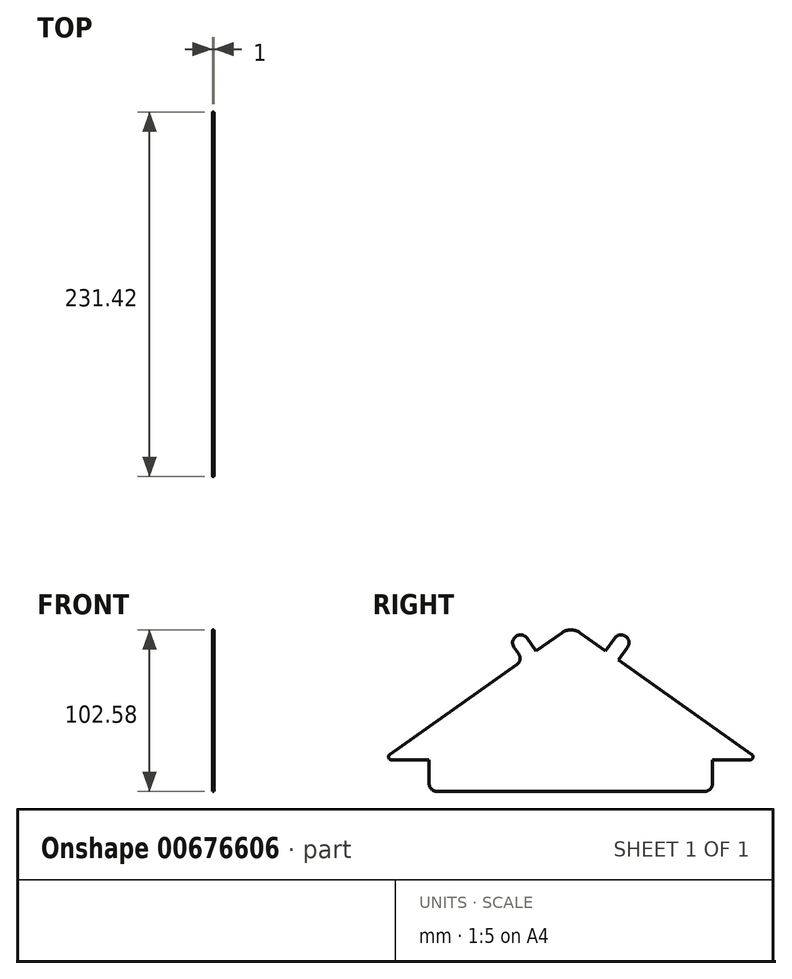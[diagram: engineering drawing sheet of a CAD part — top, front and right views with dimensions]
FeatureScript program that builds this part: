
annotation { "Feature Type Name" : "Feature", "Feature Type Description" : "" }
export const myFeature = defineFeature(function(context is Context, id is Id, definition is map)
    precondition{}
    {
        {
            var Q0;
            Q0=qCreatedBy(makeId("Right.planeOp"),FACE);
            var sketch = newSketch(context, id + "F0", { "sketchPlane" : qUnion([Q0])});
            skLineSegment(sketch, "E0", {"start": v(-120, 0) * mm, "end": v(120, 0) * mm, "construction": true});
            skLineSegment(sketch, "E1", {"start": v(120, 0) * mm, "end": v(0, 84.83) * mm});
            skLineSegment(sketch, "E2", {"start": v(0, 84.83) * mm, "end": v(-120, 0) * mm});
            skLineSegment(sketch, "E3", {"start": v(-120, 0) * mm, "end": v(-90, 0) * mm});
            skLineSegment(sketch, "E4", {"start": v(-90, 0) * mm, "end": v(-90, -20) * mm});
            skLineSegment(sketch, "E5", {"start": v(-90, -20) * mm, "end": v(90, -20) * mm});
            skLineSegment(sketch, "E6", {"start": v(90, -20) * mm, "end": v(90, 0) * mm});
            skLineSegment(sketch, "E7", {"start": v(90, 0) * mm, "end": v(120, 0) * mm});
            skSolve(sketch);
        }
        {
            var Q0;
            Q0 = qSketchRegion(id + "F0", true);
            extrude(context, id + "F1", {"entities" : qUnion([Q0]), "depth" : 1 * mm, "offsetDistance" : 25 * mm});
        }
        {
            var Q0;
            Q0=makeQuery(id+"F1.opExtrude","SWEPT_EDGE",EDGE,{"disambiguationData":[OSD([sQuery(id+"F0.wireOp",EDGE,"E4"),sQuery(id+"F0.wireOp",EDGE,"E5")])]});
            var Q1;
            Q1=makeQuery(id+"F1.opExtrude","SWEPT_EDGE",EDGE,{"disambiguationData":[OSD([sQuery(id+"F0.wireOp",EDGE,"E5"),sQuery(id+"F0.wireOp",EDGE,"E6")])]});
            fillet(context, id + "F2", {"entities" : qUnion([Q0, Q1]), "radius" : 5 * mm, "tangentPropagation" : true, "allowEdgeOverflow" : false});
        }
        {
            var Q0;
            Q0=makeQuery(id+"F1.opExtrude","SWEPT_EDGE",EDGE,{"disambiguationData":[OSD([sQuery(id+"F0.wireOp",EDGE,"E1"),sQuery(id+"F0.wireOp",EDGE,"E7")])]});
            var Q1;
            Q1=makeQuery(id+"F1.opExtrude","SWEPT_EDGE",EDGE,{"disambiguationData":[OSD([sQuery(id+"F0.wireOp",EDGE,"E2"),sQuery(id+"F0.wireOp",EDGE,"E3")])]});
            fillet(context, id + "F3", {"entities" : qUnion([Q0, Q1]), "radius" : 2 * mm, "tangentPropagation" : true, "allowEdgeOverflow" : false});
        }
        {
            var Q0;
            Q0=makeQuery(id+"F1.opExtrude","SWEPT_EDGE",EDGE,{"disambiguationData":[OSD([sQuery(id+"F0.wireOp",EDGE,"E1"),sQuery(id+"F0.wireOp",EDGE,"E2")])]});
            fillet(context, id + "F4", {"entities" : qUnion([Q0]), "radius" : 10 * mm, "tangentPropagation" : true, "allowEdgeOverflow" : false});
        }
        {
            var Q0;
            Q0=makeQuery(id+"F1.opExtrude","CAP_FACE",FACE,{"disambiguationData":[OSD([sQuery(id+"F0.wireOp",EDGE,"E1"),sQuery(id+"F0.wireOp",EDGE,"E2"),sQuery(id+"F0.wireOp",EDGE,"E3"),sQuery(id+"F0.wireOp",EDGE,"E4"),sQuery(id+"F0.wireOp",EDGE,"E5"),sQuery(id+"F0.wireOp",EDGE,"E6"),sQuery(id+"F0.wireOp",EDGE,"E7")])],"isStart":false});
            var sketch = newSketch(context, id + "F5", { "sketchPlane" : qUnion([Q0])});
            skLineSegment(sketch, "E8", {"start": v(-22.1, 69.2) * mm, "end": v(-27.88, 77.37) * mm});
            skLineSegment(sketch, "E9", {"start": v(-30.27, 63.43) * mm, "end": v(-36.04, 71.6) * mm});
            skArc(sketch, "E10", {"start": v(-27.88, 77.37) * mm, "mid": v(-34.85, 78.56) * mm, "end": v(-36.04, 71.6) * mm});
            skLineSegment(sketch, "E11", {"start": v(-30.27, 63.43) * mm, "end": v(-22.1, 69.2) * mm});
            skSolve(sketch);
        }
        {
            var Q0;
            Q0=makeQuery(id+"F5.imprint","IMPRINT",FACE,{"disambiguationData":[TD([[makeQuery(id+"F5.imprint","IMPRINT",EDGE,{"derivedFrom":sQuery(id+"F5.wireOp",EDGE,"E8")}),1.0]])]});
            var Q1;
            Q1=makeQuery(id+"F1.opExtrude","CAP_FACE",FACE,{"disambiguationData":[OSD([sQuery(id+"F0.wireOp",EDGE,"E1"),sQuery(id+"F0.wireOp",EDGE,"E2"),sQuery(id+"F0.wireOp",EDGE,"E3"),sQuery(id+"F0.wireOp",EDGE,"E4"),sQuery(id+"F0.wireOp",EDGE,"E5"),sQuery(id+"F0.wireOp",EDGE,"E6"),sQuery(id+"F0.wireOp",EDGE,"E7")])],"isStart":true});
            extrude(context, id + "F6", {"entities" : qUnion([Q0]), "operationType" : NewBodyOperationType.ADD, "endBound" : BoundingType.UP_TO_SURFACE, "oppositeDirection" : true, "depth" : 25 * mm, "endBoundEntityFace" : qUnion([Q1]), "offsetDistance" : 25 * mm});
        }
        {
            var Q0;
            Q0=makeQuery(id+"F1.opExtrude","SWEPT_BODY",BODY,{"disambiguationData":[OSD([sQuery(id+"F0.wireOp",EDGE,"E1"),sQuery(id+"F0.wireOp",EDGE,"E2"),sQuery(id+"F0.wireOp",EDGE,"E3"),sQuery(id+"F0.wireOp",EDGE,"E4"),sQuery(id+"F0.wireOp",EDGE,"E5"),sQuery(id+"F0.wireOp",EDGE,"E6"),sQuery(id+"F0.wireOp",EDGE,"E7")])]});
            var Q1;
            Q1=qCreatedBy(makeId("Front.planeOp"),FACE);
            mirror(context, id + "F7", {"operationType" : NewBodyOperationType.ADD, "entities" : qUnion([Q0]), "mirrorPlane" : qUnion([Q1])});
        }
        {
            var Q0;
            Q0=makeQuery(id+"F6.opExtrude","SWEPT_EDGE",EDGE,{"disambiguationData":[OSD([sQuery(id+"F0.wireOp",EDGE,"E2"),sQuery(id+"F5.wireOp",EDGE,"E9"),sQuery(id+"F5.wireOp",EDGE,"E11")])]});
            var Q1;
            Q1=makeQuery(id+"F6.opExtrude","SWEPT_EDGE",EDGE,{"disambiguationData":[OSD([sQuery(id+"F0.wireOp",EDGE,"E2"),sQuery(id+"F5.wireOp",EDGE,"E8"),sQuery(id+"F5.wireOp",EDGE,"E11")])]});
            var Q2;
            Q2=makeQuery(id+"F7.opPattern","COPY",EDGE,{"derivedFrom":makeQuery(id+"F6.opExtrude","SWEPT_EDGE",EDGE,{"disambiguationData":[OSD([sQuery(id+"F0.wireOp",EDGE,"E2"),sQuery(id+"F5.wireOp",EDGE,"E8"),sQuery(id+"F5.wireOp",EDGE,"E11")])]}),"instanceName":"1"});
            var Q3;
            Q3=makeQuery(id+"F7.opPattern","COPY",EDGE,{"derivedFrom":makeQuery(id+"F6.opExtrude","SWEPT_EDGE",EDGE,{"disambiguationData":[OSD([sQuery(id+"F0.wireOp",EDGE,"E2"),sQuery(id+"F5.wireOp",EDGE,"E9"),sQuery(id+"F5.wireOp",EDGE,"E11")])]}),"instanceName":"1"});
            fillet(context, id + "F8", {"entities" : qUnion([Q0, Q1, Q2, Q3]), "radius" : 5 * mm, "tangentPropagation" : true, "allowEdgeOverflow" : false});
        }
    });
